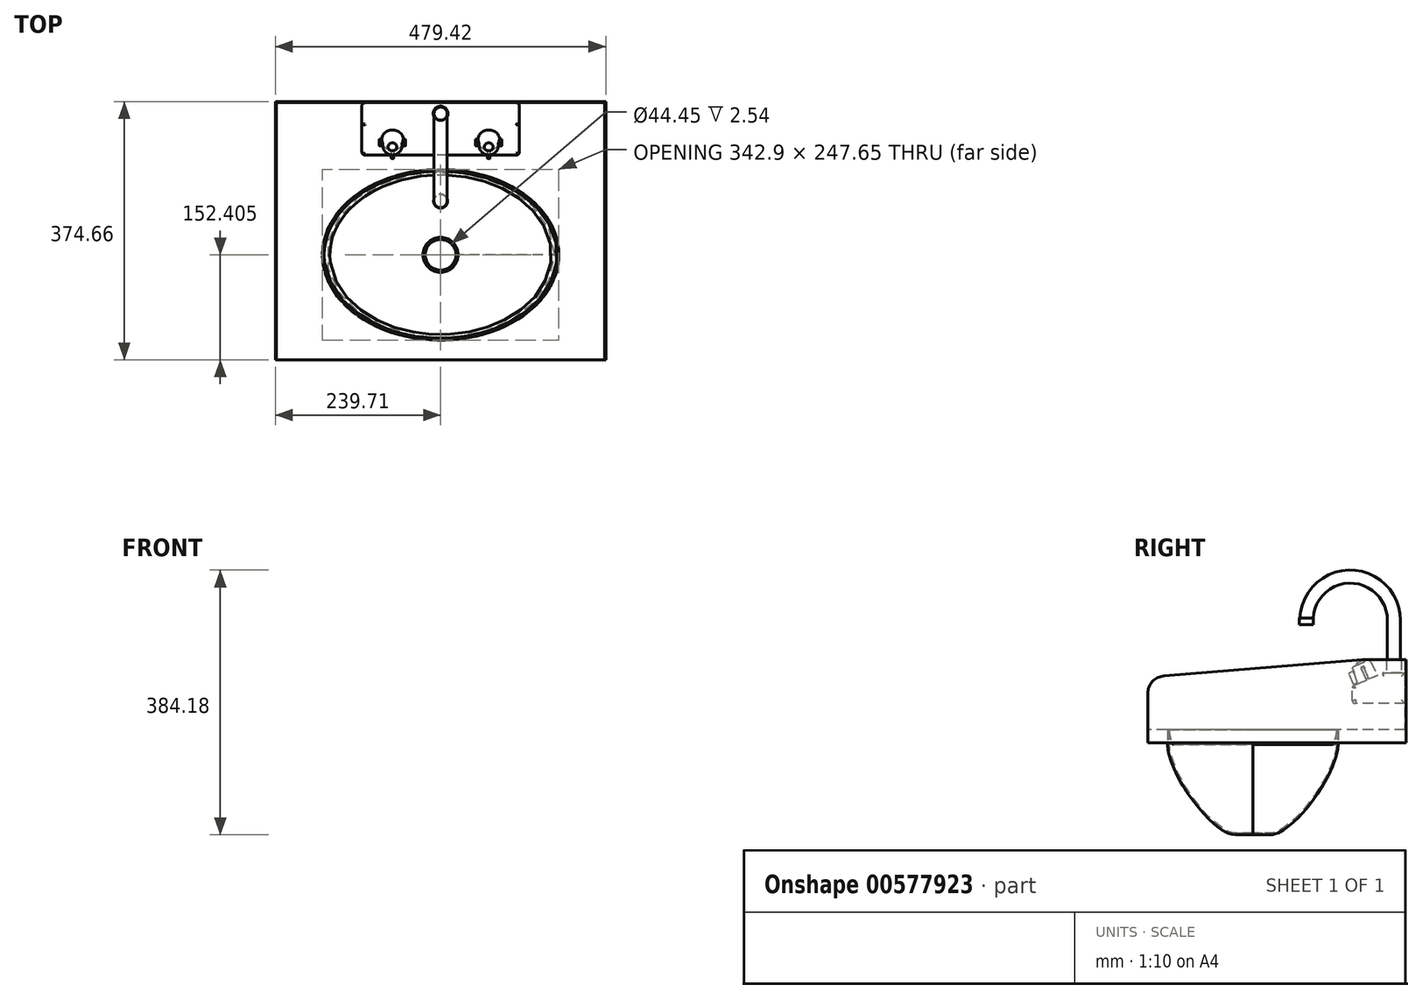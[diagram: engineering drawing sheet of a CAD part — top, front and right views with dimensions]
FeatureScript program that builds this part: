
annotation { "Feature Type Name" : "Feature", "Feature Type Description" : "" }
export const myFeature = defineFeature(function(context is Context, id is Id, definition is map)
    precondition{}
    {
        {
            var Q0;
            Q0=qCreatedBy(makeId("Top.planeOp"),FACE);
            var sketch = newSketch(context, id + "F0", { "sketchPlane" : qUnion([Q0])});
            skLineSegment(sketch, "E0.bottom", {"start": v(239.71, 187.33) * mm, "end": v(-239.71, 187.33) * mm});
            skLineSegment(sketch, "E0.top", {"start": v(239.71, -187.32) * mm, "end": v(-239.71, -187.32) * mm});
            skLineSegment(sketch, "E0.left", {"start": v(239.71, 187.33) * mm, "end": v(239.71, -187.32) * mm});
            skLineSegment(sketch, "E0.right", {"start": v(-239.71, 187.33) * mm, "end": v(-239.71, -187.32) * mm});
            skPoint(sketch, "E0.middle", {"position": v(0, 0) * mm});
            skSolve(sketch);
        }
        {
            var Q0;
            Q0 = qSketchRegion(id + "F0", true);
            extrude(context, id + "F1", {"entities" : qUnion([Q0]), "oppositeDirection" : true, "depth" : 19.05 * mm, "offsetDistance" : 25.4 * mm});
        }
        {
            var Q0;
            Q0=makeQuery(id+"F1.opExtrude","CAP_FACE",FACE,{"disambiguationData":[OSD([sQuery(id+"F0.wireOp",EDGE,"E0.bottom"),sQuery(id+"F0.wireOp",EDGE,"E0.top"),sQuery(id+"F0.wireOp",EDGE,"E0.left"),sQuery(id+"F0.wireOp",EDGE,"E0.right")])],"isStart":true});
            var sketch = newSketch(context, id + "F2", { "sketchPlane" : qUnion([Q0])});
            skLineSegment(sketch, "E1.0", {"start": v(-239.71, 187.33) * mm, "end": v(-239.71, -187.32) * mm});
            skLineSegment(sketch, "E1.1", {"start": v(239.71, 187.33) * mm, "end": v(-239.71, 187.33) * mm});
            skLineSegment(sketch, "E1.2", {"start": v(239.71, 187.33) * mm, "end": v(239.71, -187.32) * mm});
            skLineSegment(sketch, "E2.0", {"start": v(-238.13, 185.74) * mm, "end": v(-238.12, -187.32) * mm});
            skLineSegment(sketch, "E2.1", {"start": v(238.12, 185.74) * mm, "end": v(-238.13, 185.74) * mm});
            skLineSegment(sketch, "E2.2", {"start": v(238.12, 185.74) * mm, "end": v(238.13, -187.32) * mm});
            skLineSegment(sketch, "E3", {"start": v(-239.71, -187.32) * mm, "end": v(-238.12, -187.32) * mm});
            skLineSegment(sketch, "E4", {"start": v(239.71, -187.32) * mm, "end": v(238.13, -187.32) * mm});
            skSolve(sketch);
        }
        {
            var Q0;
            Q0 = qSketchRegion(id + "F2", true);
            extrude(context, id + "F3", {"entities" : qUnion([Q0]), "operationType" : NewBodyOperationType.ADD, "depth" : 101.6 * mm, "offsetDistance" : 25.4 * mm});
        }
        {
            var Q0;
            Q0=makeQuery(id+"F3.boolean.opBoolean","MERGE",FACE,{"derivedFrom":[makeQuery(id+"F1.opExtrude","SWEPT_FACE",FACE,{"disambiguationData":[OSD([sQuery(id+"F0.wireOp",EDGE,"E0.right")])]}),makeQuery(id+"F3.opExtrude","SWEPT_FACE",FACE,{"disambiguationData":[OSD([sQuery(id+"F2.wireOp",EDGE,"E1.0")])]})]});
            var sketch = newSketch(context, id + "F4", { "sketchPlane" : qUnion([Q0])});
            skLineSegment(sketch, "E5", {"start": v(-123.83, 101.6) * mm, "end": v(164, 78.1) * mm});
            skLineSegment(sketch, "E6", {"start": v(187.32, 52.79) * mm, "end": v(187.32, -19.05) * mm});
            skPoint(sketch, "E7.visualSharp", {"position": v(187.32, 76.2) * mm});
            skArc(sketch, "E7.filletArc", {"start": v(187.32, 52.79) * mm, "mid": v(180.6, 70) * mm, "end": v(164, 78.1) * mm});
            skLineSegment(sketch, "E8", {"start": v(-123.83, 101.6) * mm, "end": v(-123.83, 149.78) * mm});
            skLineSegment(sketch, "E9", {"start": v(-123.83, 149.78) * mm, "end": v(212.02, 149.78) * mm});
            skLineSegment(sketch, "E10", {"start": v(212.02, 149.78) * mm, "end": v(212.02, -19.05) * mm});
            skLineSegment(sketch, "E11", {"start": v(212.02, -19.05) * mm, "end": v(187.32, -19.05) * mm});
            skSolve(sketch);
        }
        {
            var Q0;
            Q0 = qSketchRegion(id + "F4", true);
            extrude(context, id + "F5", {"entities" : qUnion([Q0]), "operationType" : NewBodyOperationType.REMOVE, "endBound" : BoundingType.THROUGH_ALL, "oppositeDirection" : true, "depth" : 25.4 * mm, "offsetDistance" : 25.4 * mm});
        }
        {
            var Q0;
            Q0=makeQuery(id+"F1.opExtrude","CAP_FACE",FACE,{"disambiguationData":[OSD([sQuery(id+"F0.wireOp",EDGE,"E0.bottom"),sQuery(id+"F0.wireOp",EDGE,"E0.top"),sQuery(id+"F0.wireOp",EDGE,"E0.left"),sQuery(id+"F0.wireOp",EDGE,"E0.right")])],"isStart":true});
            var sketch = newSketch(context, id + "F6", { "sketchPlane" : qUnion([Q0])});
            skEllipse(sketch, "E12", {"center": v(0, -34.92) * mm, "majorRadius": 171.45 * mm, "minorRadius": 123.83 * mm, "majorAxis": v(1, 0)});
            skSolve(sketch);
        }
        {
            var Q0;
            Q0=makeQuery(id+"F6.imprint","IMPRINT",FACE,{"disambiguationData":[TD([[makeQuery(id+"F6.imprint","IMPRINT",EDGE,{"derivedFrom":sQuery(id+"F6.wireOp",EDGE,"E12")}),-1.0]])]});
            cPlane(context, id + "F7", {"entities" : qUnion([Q0]), "cplaneType" : CPlaneType.OFFSET, "offset" : 152.4 * mm, "oppositeDirection" : true, "width" : 152.4 * mm, "height" : 152.4 * mm});
        }
        {
            var Q0;
            Q0=qCreatedBy(id+"F7.planeOp",FACE);
            var sketch = newSketch(context, id + "F8", { "sketchPlane" : qUnion([Q0])});
            skPoint(sketch, "E13.0", {"position": v(0, -34.92) * mm});
            skCircle(sketch, "E14", {"center": v(0, -34.92) * mm, "radius": 25.4 * mm});
            skSolve(sketch);
        }
        {
            var Q0;
            Q0 = qSketchRegion(id + "F6", true);
            extrude(context, id + "F9", {"entities" : qUnion([Q0]), "operationType" : NewBodyOperationType.REMOVE, "oppositeDirection" : true, "depth" : 25.4 * mm, "offsetDistance" : 25.4 * mm});
        }
        {
            var Q0;
            Q0=makeQuery(id+"F1.opExtrude","CAP_FACE",FACE,{"disambiguationData":[OSD([sQuery(id+"F0.wireOp",EDGE,"E0.bottom"),sQuery(id+"F0.wireOp",EDGE,"E0.top"),sQuery(id+"F0.wireOp",EDGE,"E0.left"),sQuery(id+"F0.wireOp",EDGE,"E0.right")])],"isStart":false});
            var sketch = newSketch(context, id + "F10", { "sketchPlane" : qUnion([Q0])});
            skEllipse(sketch, "E15.0", {"center": v(0, 34.92) * mm, "majorRadius": 171.45 * mm, "minorRadius": 123.83 * mm, "majorAxis": v(1, 0)});
            skSolve(sketch);
        }
        {
            var Q1;
            Q1 = qSketchRegion(id + "F6", true);
            var Q2;
            Q2 = qSketchRegion(id + "F8", true);
            loft(context, id + "F11", {"startCondition" : LoftEndDerivativeType.NORMAL_TO_PROFILE, "startMagnitude" : 1, "endCondition" : LoftEndDerivativeType.NORMAL_TO_PROFILE, "endMagnitude" : 1, "sheetProfilesArray" : [{ "sheetProfileEntities" : qUnion([Q1]) }, { "sheetProfileEntities" : qUnion([Q2]) }]});
        }
        {
            var Q1;
            Q1 = qSketchRegion(id + "F10", true);
            var Q2;
            Q2 = qSketchRegion(id + "F8", true);
            loft(context, id + "F12", {"operationType" : NewBodyOperationType.ADD, "startCondition" : LoftEndDerivativeType.NORMAL_TO_PROFILE, "startMagnitude" : 1, "endCondition" : LoftEndDerivativeType.TANGENT_TO_PROFILE, "endMagnitude" : 1, "sheetProfilesArray" : [{ "sheetProfileEntities" : qUnion([Q1]) }, { "sheetProfileEntities" : qUnion([Q2]) }]});
        }
        {
            var Q0;
            Q0=makeQuery(id+"F11.opLoft","CAP_FACE",FACE,{"disambiguationData":[OSD([makeQuery(id+"F6.imprint","IMPRINT",FACE,{"disambiguationData":[TD([[makeQuery(id+"F6.imprint","IMPRINT",EDGE,{"derivedFrom":sQuery(id+"F6.wireOp",EDGE,"E12")}),1.0]])]})])],"isStart":true});
            shell(context, id + "F13", {"entities" : qUnion([Q0]), "thickness" : 2.54 * mm});
        }
        {
            var Q0;
            Q0=qCreatedBy(makeId("Right.planeOp"),FACE);
            var sketch = newSketch(context, id + "F14", { "sketchPlane" : qUnion([Q0])});
            skLineSegment(sketch, "E16", {"start": v(185.74, 38.1) * mm, "end": v(113.35, 38.1) * mm});
            skLineSegment(sketch, "E17", {"start": v(109.54, 41.91) * mm, "end": v(109.54, 60.99) * mm});
            skLineSegment(sketch, "E18", {"start": v(111.85, 64.49) * mm, "end": v(153.27, 82.24) * mm});
            skLineSegment(sketch, "E19", {"start": v(154.77, 82.55) * mm, "end": v(185.74, 82.55) * mm});
            skLineSegment(sketch, "E20", {"start": v(185.74, 101.6) * mm, "end": v(185.74, 0) * mm});
            skPoint(sketch, "E21.visualSharp", {"position": v(153.99, 82.55) * mm});
            skArc(sketch, "E21.filletArc", {"start": v(154.77, 82.55) * mm, "mid": v(154, 82.47) * mm, "end": v(153.27, 82.24) * mm});
            skPoint(sketch, "E22.visualSharp", {"position": v(109.54, 63.5) * mm});
            skArc(sketch, "E22.filletArc", {"start": v(111.85, 64.49) * mm, "mid": v(110.17, 63.09) * mm, "end": v(109.54, 60.99) * mm});
            skPoint(sketch, "E23.visualSharp", {"position": v(109.54, 38.1) * mm});
            skArc(sketch, "E23.filletArc", {"start": v(109.54, 41.91) * mm, "mid": v(110.65, 39.22) * mm, "end": v(113.35, 38.1) * mm});
            skSolve(sketch);
        }
        {
            var Q0;
            Q0 = qSketchRegion(id + "F14", true);
            extrude(context, id + "F15", {"entities" : qUnion([Q0]), "depth" : 228.6 * mm, "offsetDistance" : 25.4 * mm, "symmetric" : true});
        }
        {
            var Q0;
            Q0=makeQuery(id+"F15.opExtrude","CAP_FACE",FACE,{"disambiguationData":[OSD([sQuery(id+"F14.wireOp",EDGE,"E16"),sQuery(id+"F14.wireOp",EDGE,"E17"),sQuery(id+"F14.wireOp",EDGE,"E18"),sQuery(id+"F14.wireOp",EDGE,"E19"),sQuery(id+"F14.wireOp",EDGE,"E20"),sQuery(id+"F14.wireOp",EDGE,"E21.filletArc"),sQuery(id+"F14.wireOp",EDGE,"E22.filletArc"),sQuery(id+"F14.wireOp",EDGE,"E23.filletArc")])],"isStart":true});
            var Q1;
            Q1=makeQuery(id+"F15.opExtrude","SWEPT_FACE",FACE,{"disambiguationData":[OSD([sQuery(id+"F14.wireOp",EDGE,"E18")])]});
            var Q2;
            Q2=makeQuery(id+"F15.opExtrude","CAP_EDGE",EDGE,{"disambiguationData":[OSD([sQuery(id+"F14.wireOp",EDGE,"E20")])],"isStart":false});
            fillet(context, id + "F16", {"entities" : qUnion([Q0, Q1, Q2]), "radius" : 5.08 * mm, "tangentPropagation" : true, "allowEdgeOverflow" : false});
        }
        {
            var Q0;
            Q0=makeQuery(id+"F15.opExtrude","SWEPT_FACE",FACE,{"disambiguationData":[OSD([sQuery(id+"F14.wireOp",EDGE,"E19")])]});
            var sketch = newSketch(context, id + "F17", { "sketchPlane" : qUnion([Q0])});
            skCircle(sketch, "E24", {"center": v(0, 169.86) * mm, "radius": 9.53 * mm});
            skSolve(sketch);
        }
        {
            var Q0;
            Q0=qCreatedBy(makeId("Right.planeOp"),FACE);
            var sketch = newSketch(context, id + "F18", { "sketchPlane" : qUnion([Q0])});
            skPoint(sketch, "E25.0", {"position": v(169.86, 82.55) * mm});
            skLineSegment(sketch, "E26", {"start": v(169.86, 82.55) * mm, "end": v(169.86, 158.75) * mm});
            skArc(sketch, "E27", {"start": v(169.86, 158.75) * mm, "mid": v(106.36, 222.25) * mm, "end": v(42.86, 158.75) * mm});
            skLineSegment(sketch, "E28", {"start": v(169.86, 158.75) * mm, "end": v(42.86, 158.75) * mm, "construction": true});
            skSolve(sketch);
        }
        {
            var Q0;
            Q0 = qSketchRegion(id + "F17", true);
            var Q1;
            Q1 = qConstructionFilter(qBodyType(qCreatedBy(id + "F18" ,EDGE), BodyType.WIRE), ConstructionObject.NO);
            sweep(context, id + "F19", {"operationType" : NewBodyOperationType.ADD, "profiles" : qUnion([Q0]), "path" : qUnion([Q1])});
        }
        {
            var Q0;
            Q0=makeQuery(id+"F19.opSweep","CAP_FACE",FACE,{"disambiguationData":[OSD([sQuery(id+"F17.wireOp",EDGE,"E24"),sQuery(id+"F18.wireOp",VERTEX,"E27.end")])],"isStart":false});
            var sketch = newSketch(context, id + "F20", { "sketchPlane" : qUnion([Q0])});
            skCircle(sketch, "E29", {"center": v(0, -42.86) * mm, "radius": 10.16 * mm});
            skSolve(sketch);
        }
        {
            var Q0;
            Q0 = qSketchRegion(id + "F20", true);
            extrude(context, id + "F21", {"entities" : qUnion([Q0]), "operationType" : NewBodyOperationType.ADD, "depth" : 6.35 * mm, "offsetDistance" : 25.4 * mm, "hasSecondDirection" : true, "secondDirectionOppositeDirection" : true, "secondDirectionDepth" : 3.17 * mm});
        }
        {
            var Q0;
            Q0=makeQuery(id+"F15.opExtrude","SWEPT_FACE",FACE,{"disambiguationData":[OSD([sQuery(id+"F14.wireOp",EDGE,"E18")])]});
            var sketch = newSketch(context, id + "F22", { "sketchPlane" : qUnion([Q0])});
            skCircle(sketch, "E30", {"center": v(-69.85, 149.8) * mm, "radius": 15.88 * mm});
            skLineSegment(sketch, "E31", {"start": v(0, 128.2) * mm, "end": v(0, 138.51) * mm, "construction": true});
            skPoint(sketch, "E31.endSnap0", {"position": v(0, 128.2) * mm});
            skCircle(sketch, "E32.MirrorC", {"center": v(69.85, 149.8) * mm, "radius": 15.88 * mm});
            skSolve(sketch);
        }
        {
            var Q0;
            Q0 = qSketchRegion(id + "F22", true);
            extrude(context, id + "F23", {"entities" : qUnion([Q0]), "depth" : 25.4 * mm, "offsetDistance" : 25.4 * mm, "hasDraft" : true, "draftAngle" : 5 * degree, "draftPullDirection" : true});
        }
        {
            var Q0;
            Q0=makeQuery(id+"F23.opExtrude","CAP_FACE",FACE,{"disambiguationData":[OSD([sQuery(id+"F22.wireOp",EDGE,"E30")])],"isStart":false});
            var sketch = newSketch(context, id + "F24", { "sketchPlane" : qUnion([Q0])});
            skCircle(sketch, "E33", {"center": v(-69.85, 149.8) * mm, "radius": 6.35 * mm});
            skCircle(sketch, "E34.MirrorC", {"center": v(69.85, 149.8) * mm, "radius": 6.35 * mm});
            skSolve(sketch);
        }
        {
            var Q0;
            Q0 = qSketchRegion(id + "F24", true);
            extrude(context, id + "F25", {"entities" : qUnion([Q0]), "depth" : 3.17 * mm, "offsetDistance" : 25.4 * mm, "hasDraft" : true, "draftAngle" : 25 * degree, "draftPullDirection" : true});
        }
        {
            var Q0;
            Q0=makeQuery(id+"F23.opExtrude","CAP_FACE",FACE,{"disambiguationData":[OSD([sQuery(id+"F22.wireOp",EDGE,"E30")])],"isStart":false});
            cPlane(context, id + "F26", {"entities" : qUnion([Q0]), "cplaneType" : CPlaneType.OFFSET, "offset" : 6.35 * mm, "oppositeDirection" : true, "width" : 152.4 * mm, "height" : 152.4 * mm});
        }
        {
            var Q0;
            Q0=qCreatedBy(id+"F26.planeOp",FACE);
            var sketch = newSketch(context, id + "F27", { "sketchPlane" : qUnion([Q0])});
            skCircle(sketch, "E35", {"center": v(-69.85, 149.8) * mm, "radius": 14.2 * mm, "construction": true});
            skCircle(sketch, "E36", {"center": v(69.85, 149.8) * mm, "radius": 14.2 * mm, "construction": true});
            skLineSegment(sketch, "E37.bottom", {"start": v(-71.76, 138.37) * mm, "end": v(-67.94, 138.37) * mm});
            skLineSegment(sketch, "E37.top", {"start": v(-71, 128.2) * mm, "end": v(-68.7, 128.2) * mm});
            skLineSegment(sketch, "E37.left", {"start": v(-71.76, 138.37) * mm, "end": v(-71.76, 128.97) * mm});
            skLineSegment(sketch, "E37.right", {"start": v(-67.94, 138.37) * mm, "end": v(-67.94, 128.97) * mm});
            skLineSegment(sketch, "E38.bottom", {"start": v(-81.28, 151.7) * mm, "end": v(-88.14, 151.7) * mm});
            skLineSegment(sketch, "E38.top", {"start": v(-81.28, 147.9) * mm, "end": v(-88.14, 147.9) * mm});
            skLineSegment(sketch, "E38.left", {"start": v(-81.28, 151.7) * mm, "end": v(-81.28, 147.9) * mm});
            skLineSegment(sketch, "E38.right", {"start": v(-88.9, 150.94) * mm, "end": v(-88.9, 148.65) * mm});
            skLineSegment(sketch, "E39.bottom", {"start": v(-58.42, 151.7) * mm, "end": v(-51.56, 151.7) * mm});
            skLineSegment(sketch, "E39.top", {"start": v(-58.42, 147.9) * mm, "end": v(-51.56, 147.9) * mm});
            skLineSegment(sketch, "E39.left", {"start": v(-58.42, 151.7) * mm, "end": v(-58.42, 147.9) * mm});
            skLineSegment(sketch, "E39.right", {"start": v(-50.8, 150.94) * mm, "end": v(-50.8, 148.65) * mm});
            skLineSegment(sketch, "E40", {"start": v(-69.85, 149.8) * mm, "end": v(-69.85, 138.37) * mm, "construction": true});
            skLineSegment(sketch, "E41", {"start": v(-69.85, 138.37) * mm, "end": v(-69.85, 149.8) * mm, "construction": true});
            skLineSegment(sketch, "E42", {"start": v(-81.28, 149.8) * mm, "end": v(-69.85, 149.8) * mm, "construction": true});
            skLineSegment(sketch, "E43", {"start": v(-58.42, 149.8) * mm, "end": v(-69.85, 149.8) * mm, "construction": true});
            skPoint(sketch, "E44.visualSharp", {"position": v(-88.9, 151.7) * mm});
            skArc(sketch, "E44.filletArc", {"start": v(-88.14, 151.7) * mm, "mid": v(-88.68, 151.48) * mm, "end": v(-88.9, 150.94) * mm});
            skPoint(sketch, "E45.visualSharp", {"position": v(-88.9, 147.9) * mm});
            skArc(sketch, "E45.filletArc", {"start": v(-88.9, 148.65) * mm, "mid": v(-88.68, 148.12) * mm, "end": v(-88.14, 147.9) * mm});
            skPoint(sketch, "E46.visualSharp", {"position": v(-71.76, 128.2) * mm});
            skArc(sketch, "E46.filletArc", {"start": v(-71.76, 128.97) * mm, "mid": v(-71.53, 128.43) * mm, "end": v(-71, 128.2) * mm});
            skPoint(sketch, "E47.visualSharp", {"position": v(-67.94, 128.2) * mm});
            skArc(sketch, "E47.filletArc", {"start": v(-68.7, 128.2) * mm, "mid": v(-68.17, 128.43) * mm, "end": v(-67.94, 128.97) * mm});
            skPoint(sketch, "E48.visualSharp", {"position": v(-50.8, 147.9) * mm});
            skArc(sketch, "E48.filletArc", {"start": v(-51.56, 147.9) * mm, "mid": v(-51.02, 148.12) * mm, "end": v(-50.8, 148.65) * mm});
            skPoint(sketch, "E49.visualSharp", {"position": v(-50.8, 151.7) * mm});
            skArc(sketch, "E49.filletArc", {"start": v(-50.8, 150.94) * mm, "mid": v(-51.02, 151.48) * mm, "end": v(-51.56, 151.7) * mm});
            skLineSegment(sketch, "E50.MirrorCS", {"start": v(71, 128.2) * mm, "end": v(68.7, 128.2) * mm});
            skArc(sketch, "E51.MirrorCS", {"start": v(50.8, 150.94) * mm, "mid": v(51.02, 151.48) * mm, "end": v(51.56, 151.7) * mm});
            skLineSegment(sketch, "E52.MirrorCS", {"start": v(50.8, 150.94) * mm, "end": v(50.8, 148.65) * mm});
            skArc(sketch, "E53.MirrorCS", {"start": v(71.76, 128.97) * mm, "mid": v(71.53, 128.43) * mm, "end": v(71, 128.2) * mm});
            skArc(sketch, "E54.MirrorCS", {"start": v(51.56, 147.9) * mm, "mid": v(51.02, 148.12) * mm, "end": v(50.8, 148.65) * mm});
            skArc(sketch, "E55.MirrorCS", {"start": v(68.7, 128.2) * mm, "mid": v(68.17, 128.43) * mm, "end": v(67.94, 128.97) * mm});
            skLineSegment(sketch, "E56.MirrorCS", {"start": v(88.9, 150.94) * mm, "end": v(88.9, 148.65) * mm});
            skArc(sketch, "E57.MirrorCS", {"start": v(88.14, 151.7) * mm, "mid": v(88.68, 151.48) * mm, "end": v(88.9, 150.94) * mm});
            skArc(sketch, "E58.MirrorCS", {"start": v(88.9, 148.65) * mm, "mid": v(88.68, 148.12) * mm, "end": v(88.14, 147.9) * mm});
            skLineSegment(sketch, "E59.MirrorCS", {"start": v(71.76, 138.37) * mm, "end": v(71.76, 128.97) * mm});
            skLineSegment(sketch, "E60.MirrorCS", {"start": v(71.76, 138.37) * mm, "end": v(67.94, 138.37) * mm});
            skLineSegment(sketch, "E61.MirrorCS", {"start": v(58.42, 151.7) * mm, "end": v(51.56, 151.7) * mm});
            skLineSegment(sketch, "E62.MirrorCS", {"start": v(58.42, 147.9) * mm, "end": v(51.56, 147.9) * mm});
            skLineSegment(sketch, "E63.MirrorCS", {"start": v(58.42, 151.7) * mm, "end": v(58.42, 147.9) * mm});
            skLineSegment(sketch, "E64.MirrorCS", {"start": v(67.94, 138.37) * mm, "end": v(67.94, 128.97) * mm});
            skLineSegment(sketch, "E65.MirrorCS", {"start": v(81.28, 151.7) * mm, "end": v(88.14, 151.7) * mm});
            skLineSegment(sketch, "E66.MirrorCS", {"start": v(81.28, 147.9) * mm, "end": v(88.14, 147.9) * mm});
            skLineSegment(sketch, "E67.MirrorCS", {"start": v(69.85, 149.8) * mm, "end": v(69.85, 138.37) * mm, "construction": true});
            skLineSegment(sketch, "E68.MirrorCS", {"start": v(81.28, 151.7) * mm, "end": v(81.28, 147.9) * mm});
            skLineSegment(sketch, "E69.MirrorCS", {"start": v(69.85, 138.37) * mm, "end": v(69.85, 149.8) * mm, "construction": true});
            skPoint(sketch, "E70.MirrorP", {"position": v(50.8, 147.9) * mm});
            skPoint(sketch, "E71.MirrorP", {"position": v(88.9, 147.9) * mm});
            skLineSegment(sketch, "E72.MirrorCS", {"start": v(81.28, 149.8) * mm, "end": v(69.85, 149.8) * mm, "construction": true});
            skPoint(sketch, "E73.MirrorP", {"position": v(71.76, 128.2) * mm});
            skPoint(sketch, "E74.MirrorP", {"position": v(67.94, 128.2) * mm});
            skPoint(sketch, "E75.MirrorP", {"position": v(50.8, 151.7) * mm});
            skLineSegment(sketch, "E76.MirrorCS", {"start": v(58.42, 149.8) * mm, "end": v(69.85, 149.8) * mm, "construction": true});
            skPoint(sketch, "E77.MirrorP", {"position": v(88.9, 151.7) * mm});
            skSolve(sketch);
        }
        {
            var Q0;
            Q0 = qSketchRegion(id + "F27", true);
            extrude(context, id + "F28", {"entities" : qUnion([Q0]), "operationType" : NewBodyOperationType.ADD, "oppositeDirection" : true, "depth" : 17.78 * mm, "offsetDistance" : 25.4 * mm});
        }
        {
            var Q0;
            Q0=makeQuery(id+"F23.opExtrude","CAP_FACE",FACE,{"disambiguationData":[OSD([sQuery(id+"F22.wireOp",EDGE,"E32.MirrorC")])],"isStart":false});
            var Q1;
            Q1=makeQuery(id+"F23.opExtrude","CAP_FACE",FACE,{"disambiguationData":[OSD([sQuery(id+"F22.wireOp",EDGE,"E30")])],"isStart":false});
            fillet(context, id + "F29", {"entities" : qUnion([Q0, Q1]), "radius" : 3.8 * mm, "tangentPropagation" : true, "allowEdgeOverflow" : false});
        }
        {
            var Q0;
            Q0=makeQuery(id+"F25.opExtrude","CAP_FACE",FACE,{"disambiguationData":[OSD([sQuery(id+"F24.wireOp",EDGE,"E34.MirrorC")])],"isStart":false});
            fillet(context, id + "F30", {"entities" : qUnion([Q0]), "radius" : 3.8 * mm, "tangentPropagation" : true, "allowEdgeOverflow" : false});
        }
        {
            var Q0;
            Q0=makeQuery(id+"F25.opExtrude","CAP_FACE",FACE,{"disambiguationData":[OSD([sQuery(id+"F24.wireOp",EDGE,"E33")])],"isStart":false});
            fillet(context, id + "F31", {"entities" : qUnion([Q0]), "radius" : 5.08 * mm, "tangentPropagation" : true, "allowEdgeOverflow" : false});
        }
        {
            var Q0;
            Q0=makeQuery(id+"F28.opExtrude","CAP_FACE",FACE,{"disambiguationData":[OSD([sQuery(id+"F27.wireOp",EDGE,"E56.MirrorCS"),sQuery(id+"F27.wireOp",EDGE,"E57.MirrorCS"),sQuery(id+"F27.wireOp",EDGE,"E58.MirrorCS"),sQuery(id+"F27.wireOp",EDGE,"E65.MirrorCS"),sQuery(id+"F27.wireOp",EDGE,"E66.MirrorCS"),sQuery(id+"F27.wireOp",EDGE,"E68.MirrorCS")])],"isStart":true});
            var Q1;
            Q1=makeQuery(id+"F28.opExtrude","CAP_FACE",FACE,{"disambiguationData":[OSD([sQuery(id+"F27.wireOp",EDGE,"E50.MirrorCS"),sQuery(id+"F27.wireOp",EDGE,"E53.MirrorCS"),sQuery(id+"F27.wireOp",EDGE,"E55.MirrorCS"),sQuery(id+"F27.wireOp",EDGE,"E59.MirrorCS"),sQuery(id+"F27.wireOp",EDGE,"E60.MirrorCS"),sQuery(id+"F27.wireOp",EDGE,"E64.MirrorCS")])],"isStart":true});
            var Q2;
            Q2=makeQuery(id+"F28.opExtrude","CAP_FACE",FACE,{"disambiguationData":[OSD([sQuery(id+"F27.wireOp",EDGE,"E51.MirrorCS"),sQuery(id+"F27.wireOp",EDGE,"E52.MirrorCS"),sQuery(id+"F27.wireOp",EDGE,"E54.MirrorCS"),sQuery(id+"F27.wireOp",EDGE,"E61.MirrorCS"),sQuery(id+"F27.wireOp",EDGE,"E62.MirrorCS"),sQuery(id+"F27.wireOp",EDGE,"E63.MirrorCS")])],"isStart":true});
            var Q3;
            Q3=makeQuery(id+"F28.opExtrude","CAP_FACE",FACE,{"disambiguationData":[OSD([sQuery(id+"F27.wireOp",EDGE,"E38.bottom"),sQuery(id+"F27.wireOp",EDGE,"E38.top"),sQuery(id+"F27.wireOp",EDGE,"E38.left"),sQuery(id+"F27.wireOp",EDGE,"E38.right"),sQuery(id+"F27.wireOp",EDGE,"E44.filletArc"),sQuery(id+"F27.wireOp",EDGE,"E45.filletArc")])],"isStart":true});
            var Q4;
            Q4=makeQuery(id+"F28.opExtrude","CAP_FACE",FACE,{"disambiguationData":[OSD([sQuery(id+"F27.wireOp",EDGE,"E39.bottom"),sQuery(id+"F27.wireOp",EDGE,"E39.top"),sQuery(id+"F27.wireOp",EDGE,"E39.left"),sQuery(id+"F27.wireOp",EDGE,"E39.right"),sQuery(id+"F27.wireOp",EDGE,"E48.filletArc"),sQuery(id+"F27.wireOp",EDGE,"E49.filletArc")])],"isStart":true});
            var Q5;
            Q5=makeQuery(id+"F28.opExtrude","CAP_FACE",FACE,{"disambiguationData":[OSD([sQuery(id+"F27.wireOp",EDGE,"E37.bottom"),sQuery(id+"F27.wireOp",EDGE,"E37.top"),sQuery(id+"F27.wireOp",EDGE,"E37.left"),sQuery(id+"F27.wireOp",EDGE,"E37.right"),sQuery(id+"F27.wireOp",EDGE,"E46.filletArc"),sQuery(id+"F27.wireOp",EDGE,"E47.filletArc")])],"isStart":true});
            fillet(context, id + "F32", {"entities" : qUnion([Q0, Q1, Q2, Q3, Q4, Q5]), "radius" : 1.27 * mm, "tangentPropagation" : true, "allowEdgeOverflow" : false});
        }
        {
            var Q0;
            Q0=makeQuery(id+"F15.opExtrude","SWEPT_FACE",FACE,{"disambiguationData":[OSD([sQuery(id+"F14.wireOp",EDGE,"E19")])]});
            var sketch = newSketch(context, id + "F33", { "sketchPlane" : qUnion([Q0])});
            skCircle(sketch, "E78", {"center": v(0, 169.86) * mm, "radius": 10.8 * mm});
            skSolve(sketch);
        }
        {
            var Q0;
            Q0 = qSketchRegion(id + "F33", true);
            extrude(context, id + "F34", {"entities" : qUnion([Q0]), "operationType" : NewBodyOperationType.ADD, "depth" : 19.05 * mm, "offsetDistance" : 25.4 * mm});
        }
        {
            var Q0;
            Q0=makeQuery(id+"F11.opLoft","CAP_FACE",FACE,{"disambiguationData":[OSD([makeQuery(id+"F8.imprint","IMPRINT",FACE,{"disambiguationData":[TD([[makeQuery(id+"F8.imprint","IMPRINT",EDGE,{"derivedFrom":sQuery(id+"F8.wireOp",EDGE,"E14")}),1.0]])]})])],"isStart":true});
            var sketch = newSketch(context, id + "F35", { "sketchPlane" : qUnion([Q0])});
            skPoint(sketch, "E79.0", {"position": v(0, 34.92) * mm});
            skCircle(sketch, "E80", {"center": v(0, 34.92) * mm, "radius": 22.23 * mm});
            skSolve(sketch);
        }
        {
            var Q0;
            Q0 = qSketchRegion(id + "F35", true);
            extrude(context, id + "F36", {"entities" : qUnion([Q0]), "operationType" : NewBodyOperationType.REMOVE, "oppositeDirection" : true, "depth" : 25.4 * mm, "offsetDistance" : 25.4 * mm});
        }
    });
